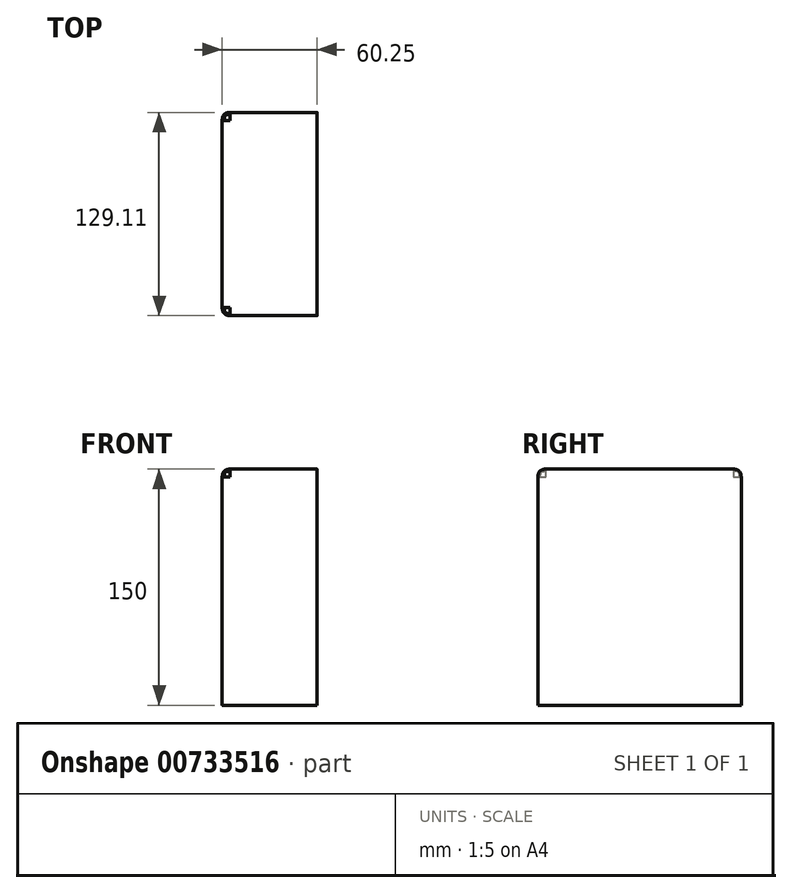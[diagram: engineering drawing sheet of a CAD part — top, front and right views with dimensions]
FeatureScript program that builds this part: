
annotation { "Feature Type Name" : "Feature", "Feature Type Description" : "" }
export const myFeature = defineFeature(function(context is Context, id is Id, definition is map)
    precondition{}
    {
        {
            var Q0;
            Q0=qCreatedBy(makeId("Top.planeOp"),FACE);
            var sketch = newSketch(context, id + "F0", { "sketchPlane" : qUnion([Q0])});
            skLineSegment(sketch, "E0.bottom", {"start": v(-60.25, 68.27) * mm, "end": v(0, 68.27) * mm});
            skLineSegment(sketch, "E0.top", {"start": v(-60.25, -60.84) * mm, "end": v(0, -60.84) * mm});
            skLineSegment(sketch, "E0.left", {"start": v(-60.25, 68.27) * mm, "end": v(-60.25, -60.84) * mm});
            skLineSegment(sketch, "E0.right", {"start": v(0, 68.27) * mm, "end": v(0, -60.84) * mm});
            skSolve(sketch);
        }
        {
            var Q0;
            Q0=makeQuery(id+"F0.imprint","IMPRINT",FACE,{"disambiguationData":[TD([[makeQuery(id+"F0.imprint","IMPRINT",EDGE,{"derivedFrom":sQuery(id+"F0.wireOp",EDGE,"E0.bottom")}),-1.0]])]});
            extrude(context, id + "F1", {"entities" : qUnion([Q0]), "endBound" : BoundingType.SYMMETRIC, "depth" : 150 * mm, "offsetDistance" : 25.4 * mm});
        }
        {
            var Q0;
            Q0=makeQuery(id+"F1.opExtrude","CAP_EDGE",EDGE,{"disambiguationData":[OSD([sQuery(id+"F0.wireOp",EDGE,"E0.left")])],"isStart":false});
            var Q1;
            Q1=makeQuery(id+"F1.opExtrude","CAP_EDGE",EDGE,{"disambiguationData":[OSD([sQuery(id+"F0.wireOp",EDGE,"E0.top")])],"isStart":false});
            var Q2;
            Q2=makeQuery(id+"F1.opExtrude","CAP_EDGE",EDGE,{"disambiguationData":[OSD([sQuery(id+"F0.wireOp",EDGE,"E0.bottom")])],"isStart":false});
            var Q3;
            Q3=makeQuery(id+"F1.opExtrude","SWEPT_EDGE",EDGE,{"disambiguationData":[OSD([sQuery(id+"F0.wireOp",EDGE,"E0.top"),sQuery(id+"F0.wireOp",EDGE,"E0.left")])]});
            var Q4;
            Q4=makeQuery(id+"F1.opExtrude","SWEPT_EDGE",EDGE,{"disambiguationData":[OSD([sQuery(id+"F0.wireOp",EDGE,"E0.bottom"),sQuery(id+"F0.wireOp",EDGE,"E0.left")])]});
            fillet(context, id + "F2", {"entities" : qUnion([Q0, Q1, Q2, Q3, Q4]), "radius" : 5.08 * mm, "rho" : 0.5, "crossSection" : FilletCrossSection.CONIC, "allowEdgeOverflow" : false});
        }
    });
